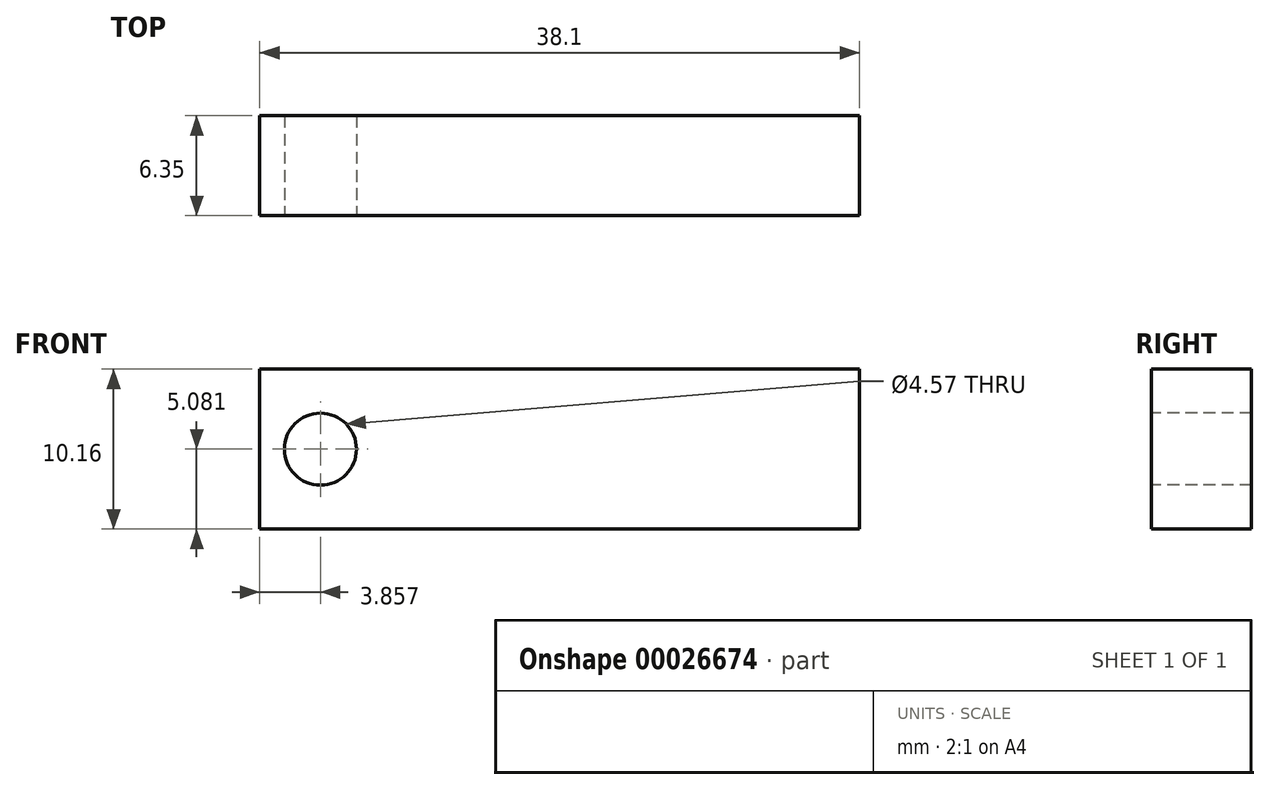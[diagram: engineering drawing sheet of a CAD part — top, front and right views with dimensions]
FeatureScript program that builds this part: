
annotation { "Feature Type Name" : "Feature", "Feature Type Description" : "" }
export const myFeature = defineFeature(function(context is Context, id is Id, definition is map)
    precondition{}
    {
        {
            var Q0;
            Q0=qCreatedBy(makeId("Front.planeOp"),FACE);
            var sketch = newSketch(context, id + "F0", { "sketchPlane" : qUnion([Q0])});
            skLineSegment(sketch, "E0.bottom", {"start": v(-21.08, 0.22) * mm, "end": v(17.02, 0.22) * mm});
            skLineSegment(sketch, "E0.top", {"start": v(-21.08, -9.94) * mm, "end": v(17.02, -9.94) * mm});
            skLineSegment(sketch, "E0.left", {"start": v(-21.08, 0.22) * mm, "end": v(-21.08, -9.94) * mm});
            skLineSegment(sketch, "E0.right", {"start": v(17.02, 0.22) * mm, "end": v(17.02, -9.94) * mm});
            skSolve(sketch);
        }
        {
            var Q0;
            Q0=qSketchRegion(id+"F0",true);
            extrude(context, id + "F1", {"entities" : qUnion([Q0]), "depth" : 6.35 * mm});
        }
        {
            var Q0;
            Q0=makeQuery(id+"F1.opExtrude","CAP_FACE",FACE,{"disambiguationData":[OSD([sQuery(id+"F0.wireOp",EDGE,"E0.bottom"),sQuery(id+"F0.wireOp",EDGE,"E0.top"),sQuery(id+"F0.wireOp",EDGE,"E0.left"),sQuery(id+"F0.wireOp",EDGE,"E0.right")])],"isStart":false});
            var sketch = newSketch(context, id + "F2", { "sketchPlane" : qUnion([Q0])});
            skCircle(sketch, "E1", {"center": v(-17.22, -4.86) * mm, "radius": 2.29 * mm});
            skSolve(sketch);
        }
        {
            var Q0;
            Q0=qSketchRegion(id+"F2",true);
            extrude(context, id + "F3", {"entities" : qUnion([Q0]), "operationType" : NewBodyOperationType.REMOVE, "oppositeDirection" : true, "depth" : 25.4 * mm});
        }
    });
